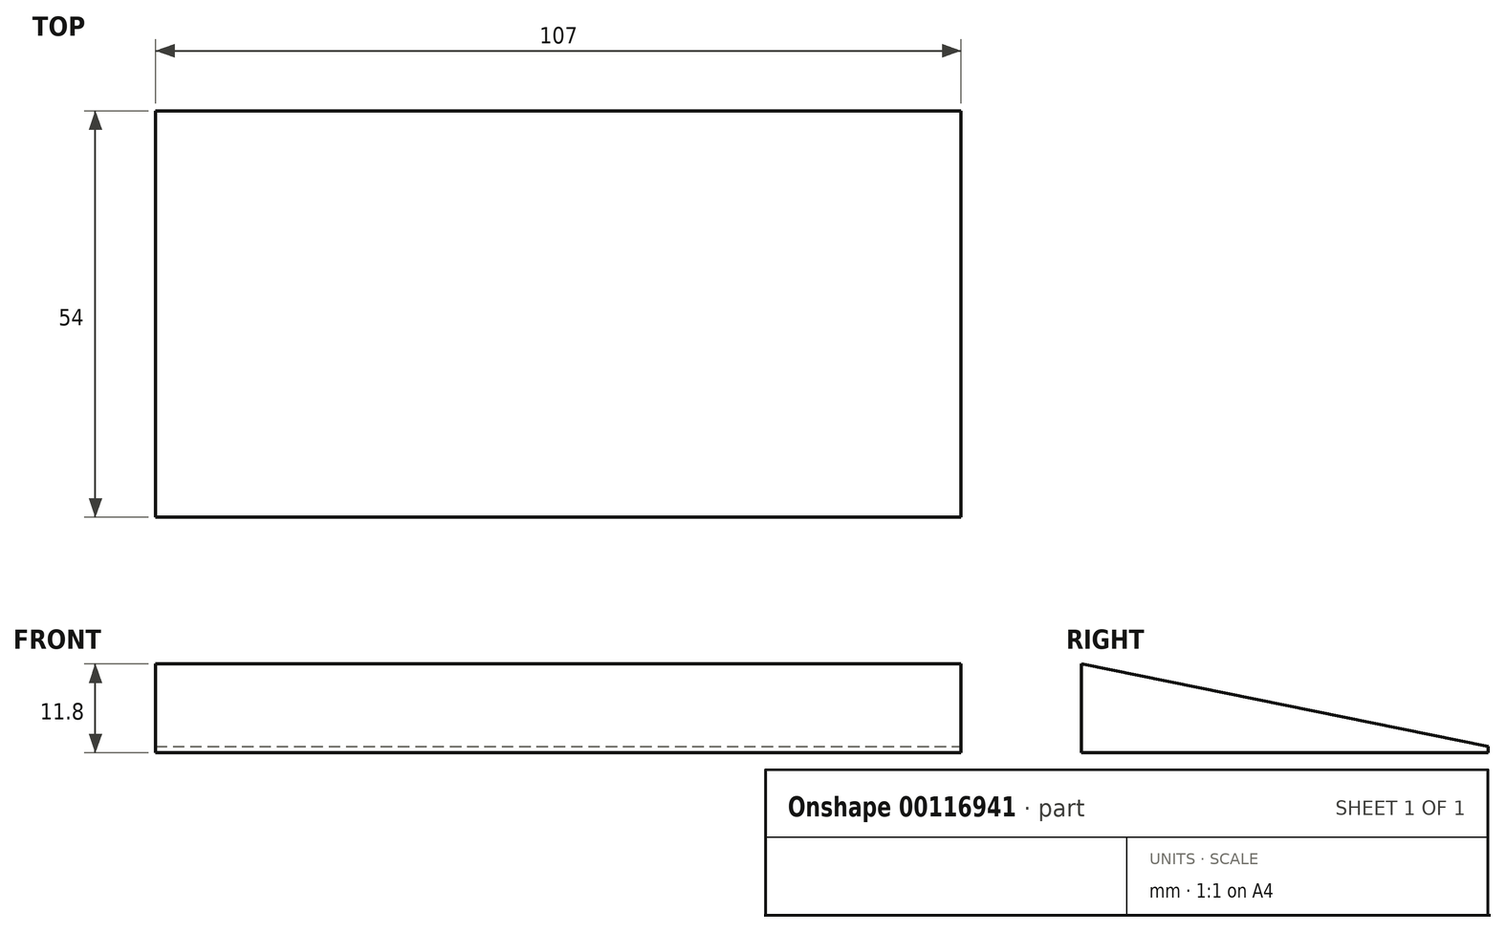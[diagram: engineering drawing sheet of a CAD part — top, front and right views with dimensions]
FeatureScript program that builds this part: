
annotation { "Feature Type Name" : "Feature", "Feature Type Description" : "" }
export const myFeature = defineFeature(function(context is Context, id is Id, definition is map)
    precondition{}
    {
        {
            var Q0;
            Q0=qCreatedBy(makeId("Top.planeOp"),FACE);
            var sketch = newSketch(context, id + "F0", { "sketchPlane" : qUnion([Q0])});
            skLineSegment(sketch, "E0.bottom", {"start": v(0, 0) * mm, "end": v(107, 0) * mm});
            skLineSegment(sketch, "E0.top", {"start": v(0, -54) * mm, "end": v(107, -54) * mm});
            skLineSegment(sketch, "E0.left", {"start": v(0, 0) * mm, "end": v(0, -54) * mm});
            skLineSegment(sketch, "E0.right", {"start": v(107, 0) * mm, "end": v(107, -54) * mm});
            skSolve(sketch);
        }
        {
            var Q0;
            Q0=makeQuery(id+"F0.imprint","IMPRINT",FACE,{"disambiguationData":[TD([[makeQuery(id+"F0.imprint","IMPRINT",EDGE,{"derivedFrom":sQuery(id+"F0.wireOp",EDGE,"E0.bottom")}),-1.0]])]});
            extrude(context, id + "F1", {"entities" : qUnion([Q0]), "depth" : 11.8 * mm});
        }
        {
            var Q0;
            Q0=makeQuery(id+"F1.opExtrude","CAP_EDGE",EDGE,{"disambiguationData":[OSD([sQuery(id+"F0.wireOp",EDGE,"E0.bottom")])],"isStart":false});
            chamfer(context, id + "F2", {"entities" : qUnion([Q0]), "chamferType" : ChamferType.OFFSET_ANGLE, "width" : 54 * mm, "oppositeDirection" : true, "angle" : 11.5 * degree});
        }
    });
